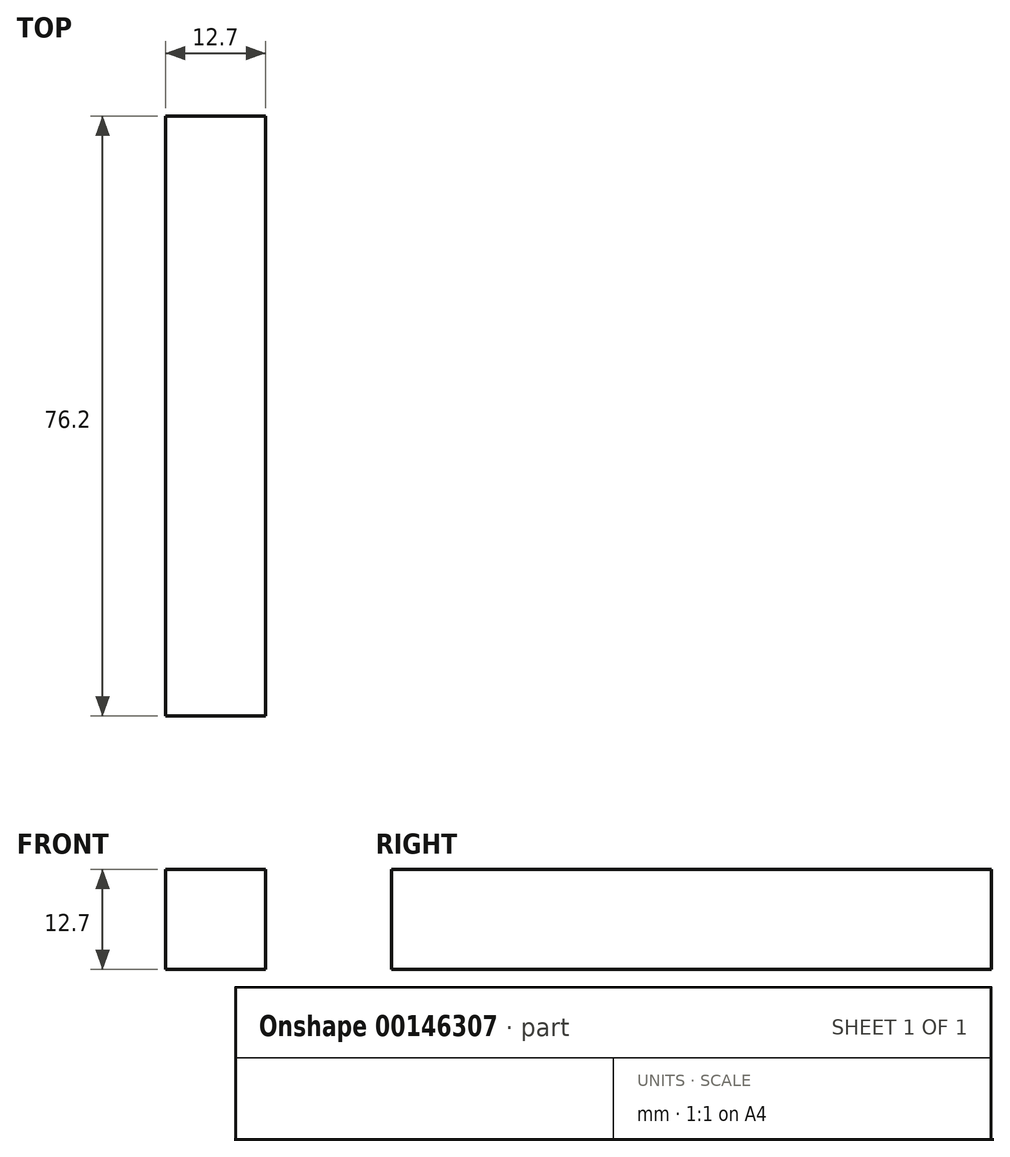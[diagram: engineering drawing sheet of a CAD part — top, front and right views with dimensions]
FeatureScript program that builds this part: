
annotation { "Feature Type Name" : "Feature", "Feature Type Description" : "" }
export const myFeature = defineFeature(function(context is Context, id is Id, definition is map)
    precondition{}
    {
        {
            var Q0;
            Q0=qCreatedBy(makeId("Front.planeOp"),FACE);
            var sketch = newSketch(context, id + "F0", { "sketchPlane" : qUnion([Q0])});
            skLineSegment(sketch, "E0.bottom", {"start": v(0, 0) * mm, "end": v(12.7, 0) * mm});
            skLineSegment(sketch, "E0.top", {"start": v(0, 12.7) * mm, "end": v(12.7, 12.7) * mm});
            skLineSegment(sketch, "E0.left", {"start": v(0, 0) * mm, "end": v(0, 12.7) * mm});
            skLineSegment(sketch, "E0.right", {"start": v(12.7, 0) * mm, "end": v(12.7, 12.7) * mm});
            skSolve(sketch);
        }
        {
            var Q0;
            Q0 = qSketchRegion(id + "F0", true);
            extrude(context, id + "F1", {"entities" : qUnion([Q0]), "depth" : 76.2 * mm});
        }
    });
